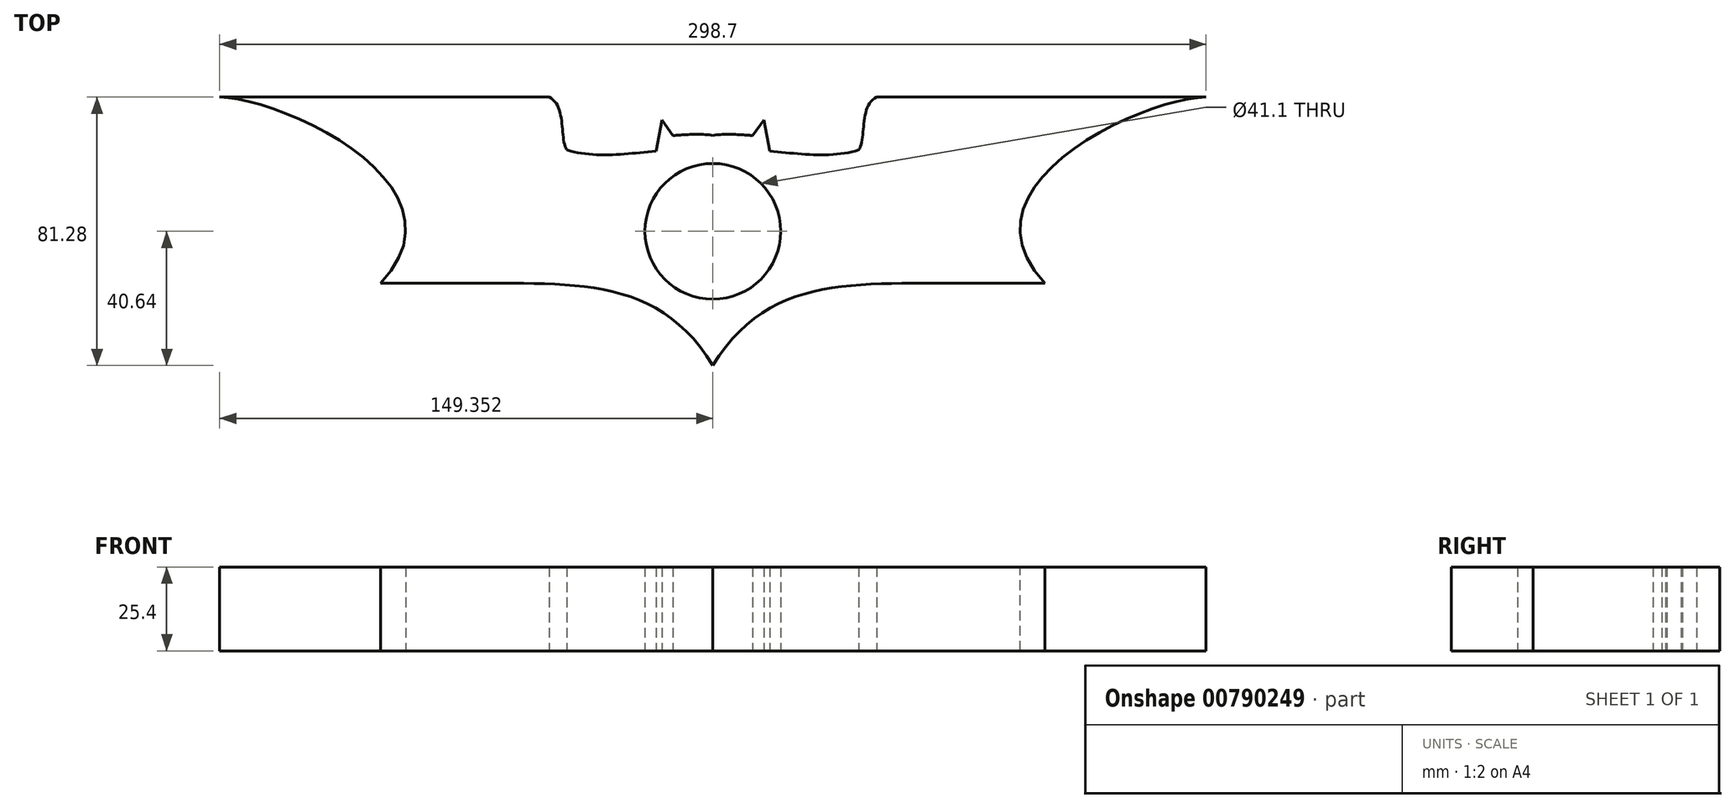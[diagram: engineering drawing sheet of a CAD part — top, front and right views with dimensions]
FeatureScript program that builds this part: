
annotation { "Feature Type Name" : "Feature", "Feature Type Description" : "" }
export const myFeature = defineFeature(function(context is Context, id is Id, definition is map)
    precondition{}
    {
        {
            var Q0;
            Q0=qCreatedBy(makeId("Top.planeOp"),FACE);
            var sketch = newSketch(context, id + "F0", { "sketchPlane" : qUnion([Q0])});
            skLineSegment(sketch, "E0.top", {"start": v(0, 81.28) * mm, "end": v(99.74, 81.28) * mm});
            skLineSegment(sketch, "E0.right", {"start": v(298.7, 0) * mm, "end": v(298.7, 81.28) * mm});
            skLineSegment(sketch, "E1", {"start": v(0, 81.28) * mm, "end": v(56.13, 81.28) * mm});
            skLineSegment(sketch, "E2", {"start": v(56.13, 0) * mm, "end": v(56.13, 81.28) * mm, "construction": true});
            skLineSegment(sketch, "E3", {"start": v(0, 81.28) * mm, "end": v(48.77, 81.28) * mm});
            skLineSegment(sketch, "E4", {"start": v(48.77, 81.28) * mm, "end": v(48.77, 0) * mm, "construction": true});
            skFitSpline(sketch, "E5", {"points": [v(0, 81.28) * mm, v(48.77, 24.9) * mm], "startDerivative": vector(54.23, 0) * mm, "endDerivative": vector(-84.75, -90.24) * mm});
            skLineSegment(sketch, "E6", {"start": v(149.35, 81.28) * mm, "end": v(149.35, 0) * mm, "construction": true});
            skLineSegment(sketch, "E7", {"start": v(48.77, 24.9) * mm, "end": v(88.9, 24.9) * mm});
            skFitSpline(sketch, "E8", {"points": [v(88.9, 24.9) * mm, v(149.35, 0) * mm], "startDerivative": vector(74.07, -0.1) * mm, "endDerivative": vector(42.75, -70.7) * mm});
            skLineSegment(sketch, "E9", {"start": v(105.16, 81.28) * mm, "end": v(105.16, 65.28) * mm, "construction": true});
            skLineSegment(sketch, "E10", {"start": v(132.11, 81.28) * mm, "end": v(132.11, 64.94) * mm, "construction": true});
            skLineSegment(sketch, "E11", {"start": v(132.11, 81.28) * mm, "end": v(131.04, 81.28) * mm});
            skFitSpline(sketch, "E12", {"points": [v(99.74, 81.28) * mm, v(105.16, 65.28) * mm], "startDerivative": vector(16.25, -7.4) * mm, "endDerivative": vector(7.1, -10.64) * mm});
            skFitSpline(sketch, "E13", {"points": [v(105.16, 65.28) * mm, v(132.11, 64.94) * mm], "startDerivative": vector(24.53, -7.67) * mm, "endDerivative": vector(27.13, 2.5) * mm});
            skLineSegment(sketch, "E14", {"start": v(132.11, 64.94) * mm, "end": v(133.94, 74.37) * mm});
            skLineSegment(sketch, "E15", {"start": v(133.94, 74.37) * mm, "end": v(137.31, 69.66) * mm});
            skPoint(sketch, "E15.endSnap0", {"position": v(133.03, 69.66) * mm});
            skFitSpline(sketch, "E16", {"points": [v(137.31, 69.66) * mm, v(149.35, 69.66) * mm], "startDerivative": vector(2.13, 0) * mm, "endDerivative": vector(11.52, -2.5) * mm});
            skLineSegment(sketch, "E17.trimOffspring", {"start": v(131.04, 81.28) * mm, "end": v(132.11, 81.28) * mm});
            skPoint(sketch, "E18.end.orphan", {"position": v(0, 24.9) * mm});
            skPoint(sketch, "E19.orphan", {"position": v(0, 0) * mm});
            skFitSpline(sketch, "E20.MirrorCS", {"points": [v(193.55, 65.28) * mm, v(166.6, 64.94) * mm], "startDerivative": vector(-24.53, -7.67) * mm, "endDerivative": vector(-27.13, 2.5) * mm});
            skLineSegment(sketch, "E21.MirrorCS", {"start": v(166.6, 64.94) * mm, "end": v(164.76, 74.37) * mm});
            skLineSegment(sketch, "E22.MirrorCS", {"start": v(164.76, 74.37) * mm, "end": v(161.4, 69.66) * mm});
            skFitSpline(sketch, "E23.MirrorCS", {"points": [v(161.4, 69.66) * mm, v(149.35, 69.66) * mm], "startDerivative": vector(-2.13, 0) * mm, "endDerivative": vector(-11.52, -2.5) * mm});
            skLineSegment(sketch, "E24.MirrorCS", {"start": v(298.7, 81.28) * mm, "end": v(198.96, 81.28) * mm});
            skFitSpline(sketch, "E25.MirrorCS", {"points": [v(298.7, 81.28) * mm, v(249.94, 24.9) * mm], "startDerivative": vector(-54.23, 0) * mm, "endDerivative": vector(84.75, -90.24) * mm});
            skLineSegment(sketch, "E26.MirrorCS", {"start": v(249.94, 24.9) * mm, "end": v(209.8, 24.9) * mm});
            skFitSpline(sketch, "E27.MirrorCS", {"points": [v(209.8, 24.9) * mm, v(149.35, 0) * mm], "startDerivative": vector(-74.07, -0.1) * mm, "endDerivative": vector(-42.75, -70.7) * mm});
            skFitSpline(sketch, "E28.MirrorCS", {"points": [v(198.96, 81.28) * mm, v(193.55, 65.28) * mm], "startDerivative": vector(-16.25, -7.4) * mm, "endDerivative": vector(-7.1, -10.64) * mm});
            skCircle(sketch, "E29", {"center": v(149.35, 40.64) * mm, "radius": 20.55 * mm});
            skLineSegment(sketch, "E30", {"start": v(0, 108.5) * mm, "end": v(298.93, 108.5) * mm});
            skSolve(sketch);
        }
        {
            var Q0;
            Q0=makeQuery(id+"F0.imprint","IMPRINT",FACE,{"disambiguationData":[TD([[makeQuery(id+"F0.imprint","IMPRINT",EDGE,{"derivedFrom":sQuery(id+"F0.wireOp",EDGE,"E0.top")}),-1.0]])]});
            extrude(context, id + "F1", {"entities" : qUnion([Q0]), "depth" : 25.4 * mm, "offsetDistance" : 25.4 * mm});
        }
    });
